FCSTD DOCUMENT  (FreeCAD 1.0R39319 (Git))
Label: session2_drawing1
License: All rights reserved
LicenseURL: https://en.wikipedia.org/wiki/All_rights_reserved
objects: Sketcher::SketchObject×1, PartDesign::Body×1
note: 3 computed .brp shape members not serialized (recipe doc carries the construction recipe); baked Part::Feature solids carry a one-line shape summary decoded from their .brp

FEATURE [Sketcher::SketchObject] Sketch
  ArcFitTolerance = 1e-06
  AttachmentSupport = -> [XY_Plane]
  FullyConstrained = true
  MakeInternals = false
  MapMode = 5
  sketch-geometry (26):
    g0: LineSegment StartX=-36 StartY=48 StartZ=0 EndX=-36 EndY=-48 EndZ=0
    g1: LineSegment StartX=-36 StartY=-48 StartZ=0 EndX=36 EndY=-48 EndZ=0
    g2: LineSegment StartX=36 StartY=-48 StartZ=0 EndX=36 EndY=48 EndZ=0
    g3: LineSegment StartX=36 StartY=48 StartZ=0 EndX=-36 EndY=48 EndZ=0
    g4: GeomPoint [constr] X=0 Y=0 Z=0
    g5: Circle CenterX=-16 CenterY=38 CenterZ=0 NormalX=0 NormalY=0 NormalZ=1 AngleXU=0 Radius=3
    g6: Circle CenterX=16 CenterY=38 CenterZ=0 NormalX=0 NormalY=0 NormalZ=1 AngleXU=0 Radius=3
    g7: ArcOfCircle CenterX=-16 CenterY=18 CenterZ=0 NormalX=0 NormalY=0 NormalZ=1 AngleXU=0 Radius=10 StartAngle=3.78304 EndAngle=5.63979
    g8: ArcOfCircle CenterX=16 CenterY=18 CenterZ=0 NormalX=0 NormalY=0 NormalZ=1 AngleXU=0 Radius=10 StartAngle=3.79224 EndAngle=5.64645
    g9: Circle CenterX=0 CenterY=-18 CenterZ=0 NormalX=0 NormalY=0 NormalZ=1 AngleXU=0 Radius=14
    g10: Circle CenterX=-26 CenterY=-18 CenterZ=0 NormalX=0 NormalY=0 NormalZ=1 AngleXU=0 Radius=3
    g11: Circle CenterX=-16 CenterY=-38 CenterZ=0 NormalX=0 NormalY=0 NormalZ=1 AngleXU=0 Radius=3
    g12: Circle CenterX=16 CenterY=-38 CenterZ=0 NormalX=0 NormalY=0 NormalZ=1 AngleXU=0 Radius=3
    g13: Circle CenterX=26 CenterY=-18 CenterZ=0 NormalX=0 NormalY=0 NormalZ=1 AngleXU=0 Radius=3
    g14: LineSegment StartX=-23.9874 StartY=24.0168 StartZ=0 EndX=-23.9874 EndY=11.9832 EndZ=0
    g15: LineSegment StartX=-7.99939 StartY=12.0008 StartZ=0 EndX=-7.99939 EndY=23.9992 EndZ=0
    g16: GeomPoint [constr] X=-16 Y=18 Z=0
    g17: LineSegment StartX=8.04309 StartY=24.057 StartZ=0 EndX=8.04309 EndY=11.943 EndZ=0
    g18: LineSegment StartX=24.0404 StartY=12.0542 StartZ=0 EndX=24.0404 EndY=23.9458 EndZ=0
    g19: GeomPoint [constr] X=16 Y=18 Z=0
    g20: GeomPoint X=8.04309 Y=24.057 Z=0
    g21: GeomPoint X=24.0404 Y=23.9458 Z=0
    g22: GeomPoint X=24.0404 Y=12.0542 Z=0
    g23: GeomPoint X=8.04309 Y=11.943 Z=0
    g24: ArcOfCircle CenterX=16 CenterY=18 CenterZ=0 NormalX=0 NormalY=0 NormalZ=1 AngleXU=0 Radius=10 StartAngle=0.636739 EndAngle=2.49094
    g25: ArcOfCircle CenterX=-16 CenterY=18 CenterZ=0 NormalX=0 NormalY=0 NormalZ=1 AngleXU=0 Radius=10 StartAngle=0.6434 EndAngle=2.49599
  constraints (70):
    c: Coincident(g0,g1)
    c: Coincident(g1,g2)
    c: Coincident(g2,g3)
    c: Coincident(g3,g0)
    c: Vertical(g0)
    c: Vertical(g2)
    c: Horizontal(g1)
    c: Horizontal(g3)
    c: Symmetric(g2,g0,g4)
    c: Coincident(g4,g-1)
    c: DistanceX(g3,g3) = 72
    c: DistanceY(g2,g2) = 96
    c: PointOnObject(g9,g-2)
    c: DistanceX(g5,g6) = 32
    c: Diameter(g5) = 6
    c: Equal(g5,g6)
    c: Distance(g5,g-2) = 16
    c: Horizontal(g5,g6)
    c: Distance(g5,g3) = 10
    c: Diameter(g7) = 20
    c: Diameter(g8) = 20
    c: Vertical(g5,g7)
    c: Vertical(g6,g8)
    c: Horizontal(g7,g8)
    c: DistanceY(g7,g5) = 20
    c: Vertical(g14)
    c: Vertical(g15)
    c: Coincident(g16,g7)
    c: Vertical(g17)
    c: Vertical(g18)
    c: Coincident(g19,g8)
    c: PointOnObject(g21,g8)
    c: PointOnObject(g18,g24)
    c: Coincident(g24,g17)
    c: Coincident(g8,g17)
    c: Coincident(g8,g18)
    c: PointOnObject(g24,g18)
    c: Coincident(g8,g24)
    c: Coincident(g20,g17)
    c: Coincident(g21,g18)
    c: Coincident(g23,g8)
    c: Coincident(g22,g8)
    c: Equal(g7,g25)
    c: Coincident(g7,g25)
    c: Coincident(g15,g25)
    c: Coincident(g14,g25)
    c: PointOnObject(g14,g7)
    c: Coincident(g15,g7)
    c: Diameter(g9) = 28
    c: DistanceY(g9,g8) = 36
    c: Diameter(g10) = 6
    c: Equal(g10,g11)
    c: Equal(g11,g12)
    c: Equal(g12,g13)
    c: DistanceY(g11,g10) = 20
    c: Distance(g11,g0) = 20
    c: Horizontal(g10,g9)
    c: Horizontal(g13,g9)
    c: Distance(g12,g-2) = 16
    c: Block(g25)
    c: Block(g7)
    c: Block(g14)
    c: Block(g15)
    c: Block(g17)
    c: Block(g8)
    c: Block(g24)
    c: Block(g18)
    c: DistanceY(g12,g13) = 20
    c: Distance(g13,g-2) = 26
    c: DistanceX(g10,g9) = 26
FEATURE [PartDesign::Body] Body
  AllowCompound = false
  Group = -> [Sketch]
  Origin = -> Origin
